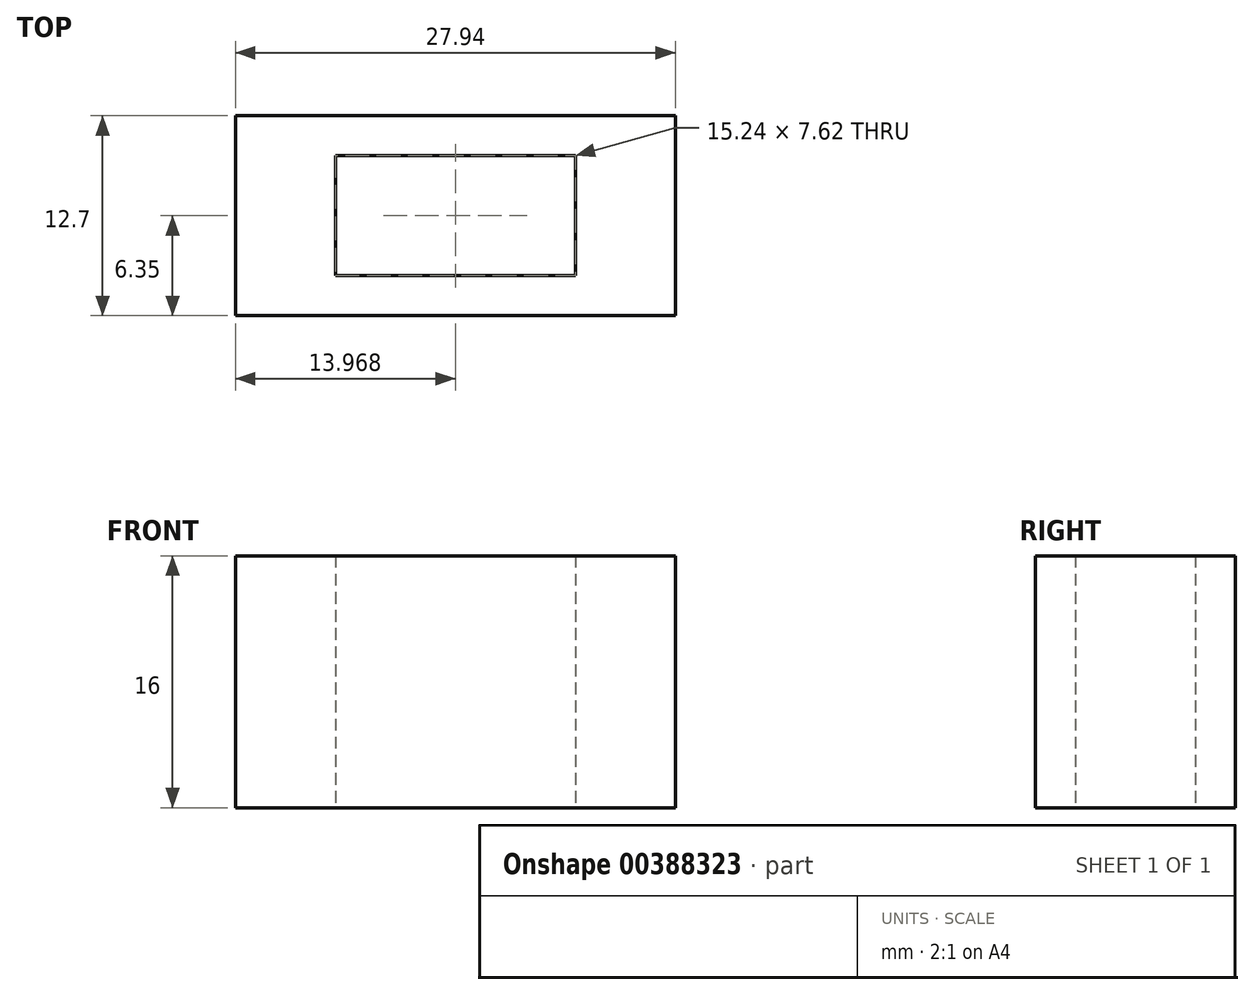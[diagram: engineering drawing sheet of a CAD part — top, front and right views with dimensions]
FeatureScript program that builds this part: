
annotation { "Feature Type Name" : "Feature", "Feature Type Description" : "" }
export const myFeature = defineFeature(function(context is Context, id is Id, definition is map)
    precondition{}
    {
        {
            var Q0;
            Q0=qCreatedBy(makeId("Front.planeOp"),FACE);
            var sketch = newSketch(context, id + "F0", { "sketchPlane" : qUnion([Q0])});
            skLineSegment(sketch, "E0", {"start": v(-6.5, 14.86) * mm, "end": v(21.44, 14.86) * mm});
            skLineSegment(sketch, "E1", {"start": v(21.44, 14.86) * mm, "end": v(21.44, -1.14) * mm});
            skLineSegment(sketch, "E2", {"start": v(21.44, -1.14) * mm, "end": v(-6.5, -1.14) * mm});
            skLineSegment(sketch, "E3", {"start": v(-6.5, -1.14) * mm, "end": v(-6.5, 14.86) * mm});
            skSolve(sketch);
        }
        {
            var Q0;
            Q0=qSketchRegion(id+"F0",true);
            extrude(context, id + "F1", {"entities" : qUnion([Q0]), "depth" : 12.7 * mm});
        }
        {
            var Q0;
            Q0=makeQuery(id+"F1.opExtrude","SWEPT_FACE",FACE,{"disambiguationData":[OSD([sQuery(id+"F0.wireOp",EDGE,"E2")])]});
            var sketch = newSketch(context, id + "F2", { "sketchPlane" : qUnion([Q0])});
            skLineSegment(sketch, "E4", {"start": v(-6.5, 6.35) * mm, "end": v(21.44, 6.35) * mm, "construction": true});
            skLineSegment(sketch, "E5", {"start": v(7.47, 12.7) * mm, "end": v(7.47, 0) * mm, "construction": true});
            skLineSegment(sketch, "E6.bottom", {"start": v(15.09, 2.54) * mm, "end": v(-0.15, 2.54) * mm});
            skLineSegment(sketch, "E6.top", {"start": v(15.09, 10.16) * mm, "end": v(-0.15, 10.16) * mm});
            skLineSegment(sketch, "E6.left", {"start": v(15.09, 2.54) * mm, "end": v(15.09, 10.16) * mm});
            skLineSegment(sketch, "E6.right", {"start": v(-0.15, 2.54) * mm, "end": v(-0.15, 10.16) * mm});
            skPoint(sketch, "E6.middle", {"position": v(7.47, 6.35) * mm});
            skSolve(sketch);
        }
        {
            var Q0;
            Q0=makeQuery(id+"F2.imprint","IMPRINT",FACE,{"disambiguationData":[TD([[makeQuery(id+"F2.imprint","IMPRINT",EDGE,{"derivedFrom":sQuery(id+"F2.wireOp",EDGE,"E6.bottom")}),-1.0]])]});
            extrude(context, id + "F3", {"entities" : qUnion([Q0]), "operationType" : NewBodyOperationType.REMOVE, "oppositeDirection" : true, "depth" : 45.83 * mm});
        }
    });
